# Revit family: P200921MX-018c_MER6600F_W
name_source: partatom
category: Specialty Equipment
units: mm (PartAtom-declared; Revit-internal decimal feet)

## family parameters
Always vertical = Yes
Cut with Voids When Loaded = No
Enable Cutting in Views = No
Maintain Annotation Orientation = No
Part Type = Normal
Room Calculation Point = No
Round Connector Dimension = Use Diameter
Shared = No
Work Plane-Based = No

## types (1)
- MER6600FW
    Accent Material = ARCAT - Plastic - Gray
    Amps = 0 A
    Back Panel Material = ARCAT - Metal - Aluminum
    Body Material = ARCAT - Metal - Steel - White
    Clearance Material = ARCAT - Clearance
    Cooktop Material = ARCAT - Glass - Tempered - Black
    Default Elevation = 0"
    Depth = 27 3/4"
    Description = 30-Inch Wide Electric Range With Shatter-Resistant Cooktop - 5.3 Cu. Ft.
30-Inch Wide Electric Range With Shatter-Resistant Cooktop - 5.3 Cu. Ft.
    Dimension Guide = http://access.whirlpool.com Guide&sku=MER6600FW&language=EN
http://access.whirlpool.com Guide&sku=MER6600FW&language=EN
    Display Panel Material = ARCAT - Glass - White
    Door Material = ARCAT - Metal - Steel - White
    Family Name = Cooking
    Feature 1 = Fingerprint Resistant Stainless Steel
Acier inoxydable résistant aux traces de doigts
    Feature 2 = Precision Cooking™ System
Système Precision Cooking™
    Feature 3 = 9"/6" Dual-Choice™ Element
Élément radiant double Dual-Choice™ de 9 po/6 po
    Glass Material = ARCAT - Glass - Black
    Handle Material = ARCAT - Metal - Steel - White
    Height = 46 7/8"
    Installation-Fabrication = https://www.whirlpool.com
https://www.whirlpool.com
    Knob Material = ARCAT - Metal - Steel - White
    LED Display Panel Material = ARCAT - Glass - Black
    Leg Material = ARCAT - Plastic - White
    Manufacturer = Maytag
    Model = MER6600FW
    Voltage = 0 V
    Width = 29 7/8"

## geometry (parser evidence)
native form markers: Sweep x5
no freeform markers — native parametric forms only
